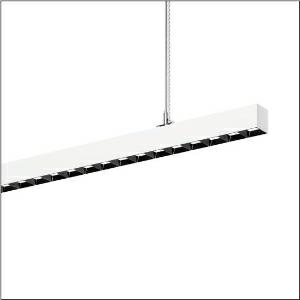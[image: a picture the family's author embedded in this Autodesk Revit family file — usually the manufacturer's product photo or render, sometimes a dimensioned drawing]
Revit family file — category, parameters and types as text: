
# Revit family: silica_21_51mx32tat7w
name_source: partatom
category: Lighting Fixtures
units: mm (PartAtom-declared; Revit-internal decimal feet)

## family parameters
Cut with Voids When Loaded = No
Host = Face
Light Source = No
Part Type = Normal
Room Calculation Point = No
Round Connector Dimension = Use Diameter
Shared = No

## types (1)
- --- (1 x LED, 6220 lm, 53.4 W, 6500K)
    Apparent Load = 53 VA
    CIE Flux Codes = 84 99 100 60 100
    Color Rendering = 80
    Color Temperature = 6500K
    Default Elevation = 1800 mm
    Description = Silica 21, office luminaire, primary light control with darklight reflector, of PMMA, black, CAT 2 (L<= 3000cd/m²), light emission: direct/indirect distribution, primary light characteristic: symmetric, installation type: suspended mounting, LED, rated luminous flux: 6.220lm, luminous efficacy: 111lm/W, light colour: 8tw, colour temperature: 2700..6500K, control gear: DALI DT8, with terminal, 3+2-pole, max. 2.5mm², mains connection: 220..240V, AC, 50/60Hz, rated input power: 56.1W, luminaire housing, of aluminium, traffic white (RAL 9016), length: 1.204mm, width: 53mm, height: 53mm, protection rating (complete): IP20, insulation class (complete): insulation class I (protective earthing), certification: CE, permissible operating ambient temperature: 0..+35°C, standard: EN 50419, packaging unit: 1 piece
    Height = 53 mm
    Lamp = 1 x LED
    Lamp Light Flux = 6220 lm
    Lamp Power = 53.4 W
    Lamp count = 1
    Length = 1204 mm
    Luminous efficacy = 116 lm/W
    Manufacturer = Siteco
    ModVariant = No
    Model = 51MX32TAT7W
    Mounting Place = Ceiling
    Mounting Type = Pendant
    Number of Poles = 1
    OnlyDefault = Yes
    Power Factor = 1
    Product Name = Silica 21
    Product group = office luminaire | ceiling pendant
    ProductGroupID = 903
    Protection Class = Protection class I
    Protection Degree = IP 20
    RLX_Detail_Level = 1
    RLX_Emergency_Light_Flux = 0 lm
    RLX_Emergency_Type = 0
    RLX_Emergency_Type_DB = No
    RlxData = <blob elided: 40577 chars, md5=2ab831a7>
    Socket = socket
    Standby Power = 0 W
    System Light Flux = 6220 lm
    System Power = 53 W
    Type Comments = individual setting
    Type Image = l_1335871.jpg
    URL = http://relux.com
    VarID = @adj_139457
    Voltage = 0 V
    Weight = 0.00 kg
    Width = 53 mm

## geometry (parser evidence)
native form markers: Blend x4, Sweep x13
no freeform markers — native parametric forms only
